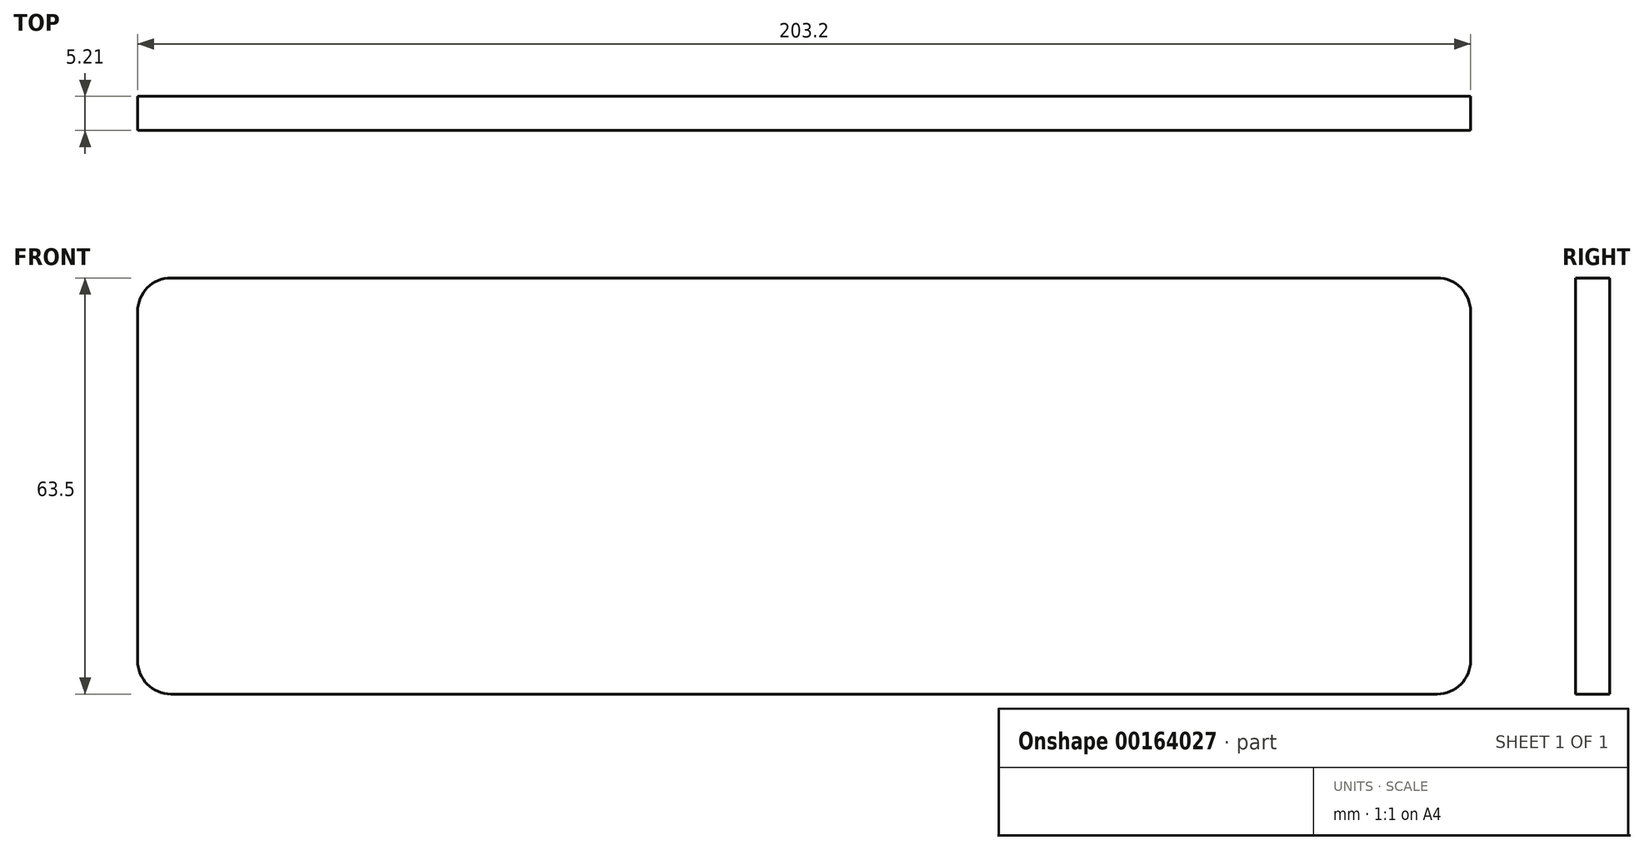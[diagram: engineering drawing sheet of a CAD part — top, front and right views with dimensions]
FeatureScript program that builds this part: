
annotation { "Feature Type Name" : "Feature", "Feature Type Description" : "" }
export const myFeature = defineFeature(function(context is Context, id is Id, definition is map)
    precondition{}
    {
        {
            var Q0;
            Q0=qCreatedBy(makeId("Front.planeOp"),FACE);
            var sketch = newSketch(context, id + "F0", { "sketchPlane" : qUnion([Q0])});
            skLineSegment(sketch, "E0.bottom", {"start": v(101.6, -31.75) * mm, "end": v(-101.6, -31.75) * mm});
            skLineSegment(sketch, "E0.top", {"start": v(101.6, 31.75) * mm, "end": v(-101.6, 31.75) * mm});
            skLineSegment(sketch, "E0.left", {"start": v(101.6, -31.75) * mm, "end": v(101.6, 31.75) * mm});
            skLineSegment(sketch, "E0.right", {"start": v(-101.6, -31.75) * mm, "end": v(-101.6, 31.75) * mm});
            skPoint(sketch, "E0.middle", {"position": v(0, 0) * mm});
            skSolve(sketch);
        }
        {
            var Q0;
            Q0=makeQuery(id+"F0.imprint","IMPRINT",FACE,{"disambiguationData":[TD([[makeQuery(id+"F0.imprint","IMPRINT",EDGE,{"derivedFrom":sQuery(id+"F0.wireOp",EDGE,"E0.bottom")}),-1.0]])]});
            extrude(context, id + "F1", {"entities" : qUnion([Q0]), "depth" : 5.2 * mm});
        }
        {
            var Q0;
            Q0=makeQuery(id+"F1.opExtrude","SWEPT_EDGE",EDGE,{"disambiguationData":[OSD([sQuery(id+"F0.wireOp",EDGE,"E0.top"),sQuery(id+"F0.wireOp",EDGE,"E0.right")])]});
            var Q1;
            Q1=makeQuery(id+"F1.opExtrude","SWEPT_EDGE",EDGE,{"disambiguationData":[OSD([sQuery(id+"F0.wireOp",EDGE,"E0.bottom"),sQuery(id+"F0.wireOp",EDGE,"E0.right")])]});
            var Q2;
            Q2=makeQuery(id+"F1.opExtrude","SWEPT_EDGE",EDGE,{"disambiguationData":[OSD([sQuery(id+"F0.wireOp",EDGE,"E0.bottom"),sQuery(id+"F0.wireOp",EDGE,"E0.left")])]});
            var Q3;
            Q3=makeQuery(id+"F1.opExtrude","SWEPT_EDGE",EDGE,{"disambiguationData":[OSD([sQuery(id+"F0.wireOp",EDGE,"E0.top"),sQuery(id+"F0.wireOp",EDGE,"E0.left")])]});
            fillet(context, id + "F2", {"entities" : qUnion([Q0, Q1, Q2, Q3]), "radius" : 5.08 * mm, "tangentPropagation" : true, "allowEdgeOverflow" : false});
        }
    });
